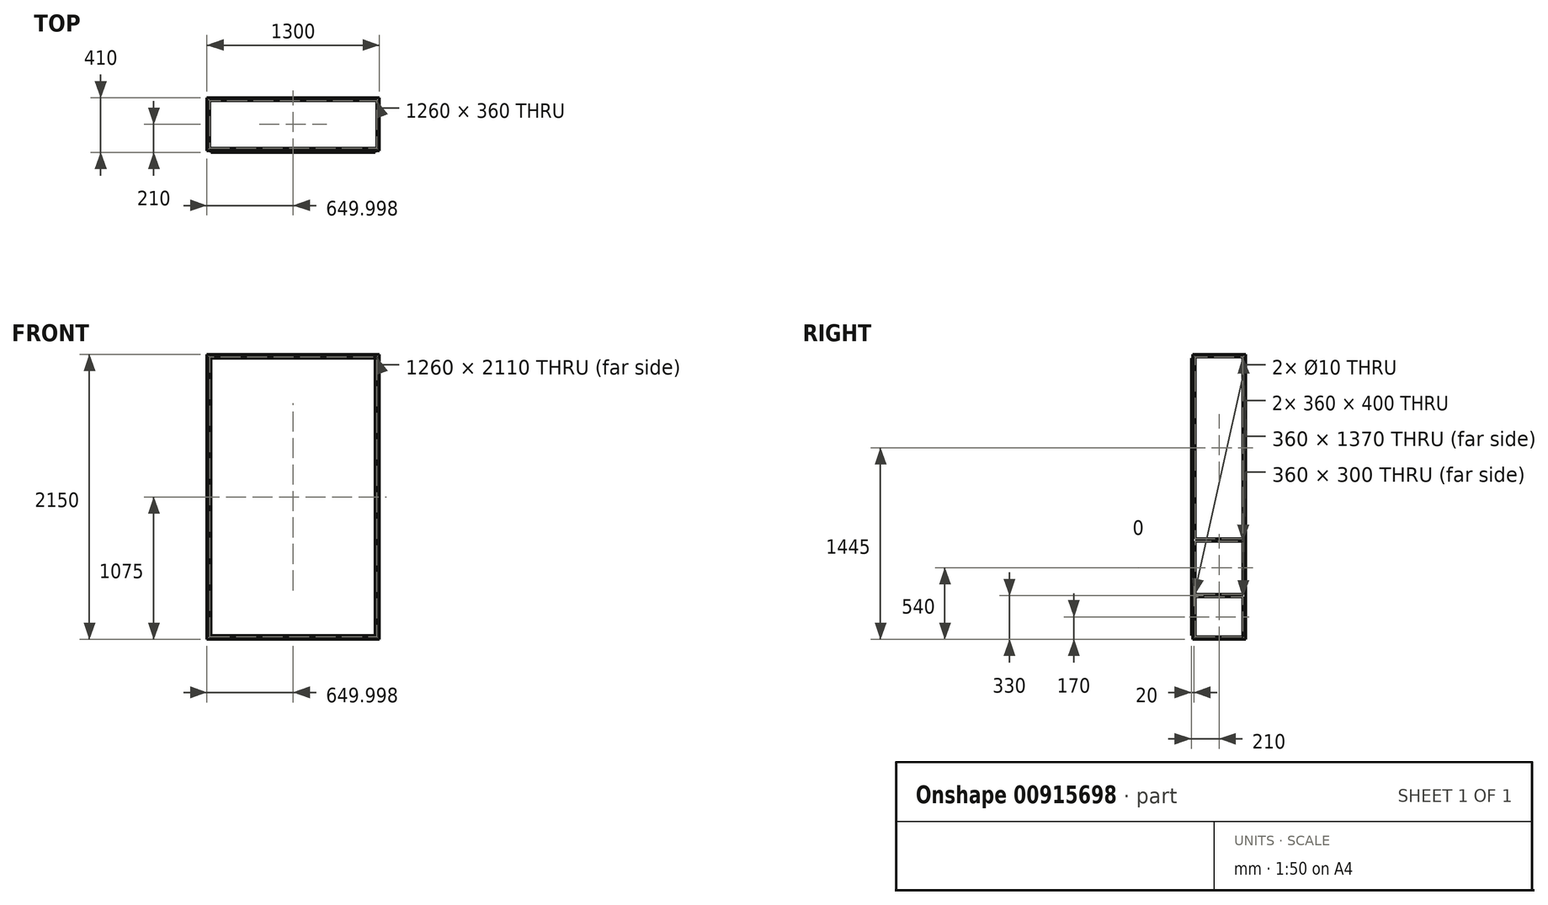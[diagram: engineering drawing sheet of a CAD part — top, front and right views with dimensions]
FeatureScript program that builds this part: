
annotation { "Feature Type Name" : "Feature", "Feature Type Description" : "" }
export const myFeature = defineFeature(function(context is Context, id is Id, definition is map)
    precondition{}
    {
        {
            var Q0;
            Q0=qCreatedBy(makeId("Front.planeOp"),FACE);
            var sketch = newSketch(context, id + "F0", { "sketchPlane" : qUnion([Q0])});
            skLineSegment(sketch, "E0", {"start": v(-54.92, 0) * mm, "end": v(1245.08, 0) * mm});
            skLineSegment(sketch, "E1", {"start": v(1245.08, 0) * mm, "end": v(1245.08, 2150) * mm});
            skLineSegment(sketch, "E2", {"start": v(1245.08, 2150) * mm, "end": v(-54.92, 2150) * mm});
            skLineSegment(sketch, "E3", {"start": v(-54.92, 0) * mm, "end": v(-54.92, 2150) * mm});
            skLineSegment(sketch, "E4.0", {"start": v(-34.92, 0) * mm, "end": v(-34.92, 2150) * mm});
            skLineSegment(sketch, "E5.0", {"start": v(1245.08, 2130) * mm, "end": v(-54.92, 2130) * mm});
            skLineSegment(sketch, "E6.0", {"start": v(1225.08, 0) * mm, "end": v(1225.08, 2150) * mm});
            skLineSegment(sketch, "E7.0", {"start": v(-54.92, 20) * mm, "end": v(1245.08, 20) * mm});
            skSolve(sketch);
        }
        {
            var Q0;
            {var subQ0=sQuery(id+"F0.wireOp",EDGE,"E4.0");var subQ1=sQuery(id+"F0.wireOp",EDGE,"E2");var subQ2=makeQuery(id+"F0.imprint","INTERSECT",VERTEX,{"derivedFrom":[subQ1,subQ0]});Q0=makeQuery(id+"F0.imprint","IMPRINT",FACE,{"disambiguationData":[TD([[makeQuery(id+"F0.imprint","IMPRINT",EDGE,{"disambiguationData":[TD([[subQ2,1.0]])],"derivedFrom":subQ1}),1.0]])]});}
            var Q1;
            {var subQ0=sQuery(id+"F0.wireOp",EDGE,"E3");var subQ1=sQuery(id+"F0.wireOp",EDGE,"E2");var subQ2=makeQuery(id+"F0.imprint","INTERSECT",VERTEX,{"derivedFrom":[subQ1,subQ0]});Q1=makeQuery(id+"F0.imprint","IMPRINT",FACE,{"disambiguationData":[TD([[makeQuery(id+"F0.imprint","IMPRINT",EDGE,{"disambiguationData":[TD([[subQ2,1.0]])],"derivedFrom":subQ1}),1.0]])]});}
            var Q2;
            {var subQ0=sQuery(id+"F0.wireOp",EDGE,"E5.0");var subQ1=sQuery(id+"F0.wireOp",EDGE,"E3");var subQ2=makeQuery(id+"F0.imprint","INTERSECT",VERTEX,{"derivedFrom":[subQ1,subQ0]});Q2=makeQuery(id+"F0.imprint","IMPRINT",FACE,{"disambiguationData":[TD([[makeQuery(id+"F0.imprint","IMPRINT",EDGE,{"disambiguationData":[TD([[subQ2,1.0]])],"derivedFrom":subQ1}),-1.0]])]});}
            var Q3;
            {var subQ0=sQuery(id+"F0.wireOp",EDGE,"E2");var subQ1=sQuery(id+"F0.wireOp",EDGE,"E1");var subQ2=makeQuery(id+"F0.imprint","INTERSECT",VERTEX,{"derivedFrom":[subQ1,subQ0]});Q3=makeQuery(id+"F0.imprint","IMPRINT",FACE,{"disambiguationData":[TD([[makeQuery(id+"F0.imprint","IMPRINT",EDGE,{"disambiguationData":[TD([[subQ2,1.0]])],"derivedFrom":subQ1}),1.0]])]});}
            var Q4;
            {var subQ0=sQuery(id+"F0.wireOp",EDGE,"E5.0");var subQ1=sQuery(id+"F0.wireOp",EDGE,"E1");var subQ2=makeQuery(id+"F0.imprint","INTERSECT",VERTEX,{"derivedFrom":[subQ1,subQ0]});Q4=makeQuery(id+"F0.imprint","IMPRINT",FACE,{"disambiguationData":[TD([[makeQuery(id+"F0.imprint","IMPRINT",EDGE,{"disambiguationData":[TD([[subQ2,1.0]])],"derivedFrom":subQ1}),1.0]])]});}
            var Q5;
            {var subQ0=sQuery(id+"F0.wireOp",EDGE,"E1");var subQ1=sQuery(id+"F0.wireOp",EDGE,"E0");var subQ2=makeQuery(id+"F0.imprint","INTERSECT",VERTEX,{"derivedFrom":[subQ1,subQ0]});Q5=makeQuery(id+"F0.imprint","IMPRINT",FACE,{"disambiguationData":[TD([[makeQuery(id+"F0.imprint","IMPRINT",EDGE,{"disambiguationData":[TD([[subQ2,1.0]])],"derivedFrom":subQ1}),1.0]])]});}
            var Q6;
            {var subQ0=sQuery(id+"F0.wireOp",EDGE,"E4.0");var subQ1=sQuery(id+"F0.wireOp",EDGE,"E0");var subQ2=makeQuery(id+"F0.imprint","INTERSECT",VERTEX,{"derivedFrom":[subQ1,subQ0]});Q6=makeQuery(id+"F0.imprint","IMPRINT",FACE,{"disambiguationData":[TD([[makeQuery(id+"F0.imprint","IMPRINT",EDGE,{"disambiguationData":[TD([[subQ2,-1.0]])],"derivedFrom":subQ1}),1.0]])]});}
            var Q7;
            {var subQ0=sQuery(id+"F0.wireOp",EDGE,"E3");var subQ1=sQuery(id+"F0.wireOp",EDGE,"E0");var subQ2=makeQuery(id+"F0.imprint","INTERSECT",VERTEX,{"derivedFrom":[subQ1,subQ0]});Q7=makeQuery(id+"F0.imprint","IMPRINT",FACE,{"disambiguationData":[TD([[makeQuery(id+"F0.imprint","IMPRINT",EDGE,{"disambiguationData":[TD([[subQ2,-1.0]])],"derivedFrom":subQ1}),1.0]])]});}
            extrude(context, id + "F1", {"entities" : qUnion([Q0, Q1, Q2, Q3, Q4, Q5, Q6, Q7]), "depth" : 20 * mm, "offsetDistance" : 25 * mm});
        }
        {
            var Q0;
            {var subQ0=sQuery(id+"F0.wireOp",EDGE,"E3");var subQ1=sQuery(id+"F0.wireOp",EDGE,"E0");var subQ2=makeQuery(id+"F0.imprint","INTERSECT",VERTEX,{"derivedFrom":[subQ1,subQ0]});Q0=makeQuery(id+"F0.imprint","IMPRINT",FACE,{"disambiguationData":[TD([[makeQuery(id+"F0.imprint","IMPRINT",EDGE,{"disambiguationData":[TD([[subQ2,-1.0]])],"derivedFrom":subQ1}),1.0]])]});}
            var Q1;
            {var subQ0=sQuery(id+"F0.wireOp",EDGE,"E1");var subQ1=sQuery(id+"F0.wireOp",EDGE,"E0");var subQ2=makeQuery(id+"F0.imprint","INTERSECT",VERTEX,{"derivedFrom":[subQ1,subQ0]});Q1=makeQuery(id+"F0.imprint","IMPRINT",FACE,{"disambiguationData":[TD([[makeQuery(id+"F0.imprint","IMPRINT",EDGE,{"disambiguationData":[TD([[subQ2,1.0]])],"derivedFrom":subQ1}),1.0]])]});}
            var Q2;
            {var subQ0=sQuery(id+"F0.wireOp",EDGE,"E3");var subQ1=sQuery(id+"F0.wireOp",EDGE,"E2");var subQ2=makeQuery(id+"F0.imprint","INTERSECT",VERTEX,{"derivedFrom":[subQ1,subQ0]});Q2=makeQuery(id+"F0.imprint","IMPRINT",FACE,{"disambiguationData":[TD([[makeQuery(id+"F0.imprint","IMPRINT",EDGE,{"disambiguationData":[TD([[subQ2,1.0]])],"derivedFrom":subQ1}),1.0]])]});}
            var Q3;
            {var subQ0=sQuery(id+"F0.wireOp",EDGE,"E2");var subQ1=sQuery(id+"F0.wireOp",EDGE,"E1");var subQ2=makeQuery(id+"F0.imprint","INTERSECT",VERTEX,{"derivedFrom":[subQ1,subQ0]});Q3=makeQuery(id+"F0.imprint","IMPRINT",FACE,{"disambiguationData":[TD([[makeQuery(id+"F0.imprint","IMPRINT",EDGE,{"disambiguationData":[TD([[subQ2,1.0]])],"derivedFrom":subQ1}),1.0]])]});}
            extrude(context, id + "F2", {"entities" : qUnion([Q0, Q1, Q2, Q3]), "operationType" : NewBodyOperationType.ADD, "depth" : 400 * mm, "offsetDistance" : 25 * mm});
        }
        {
            var Q0;
            Q0=makeQuery(id+"F2.opExtrude","CAP_FACE",FACE,{"disambiguationData":[OSD([sQuery(id+"F0.wireOp",EDGE,"E2"),sQuery(id+"F0.wireOp",EDGE,"E3"),sQuery(id+"F0.wireOp",EDGE,"E4.0"),sQuery(id+"F0.wireOp",EDGE,"E5.0")])],"isStart":false});
            var sketch = newSketch(context, id + "F3", { "sketchPlane" : qUnion([Q0])});
            skLineSegment(sketch, "E8.0", {"start": v(1245.08, 2130) * mm, "end": v(-54.92, 2130) * mm});
            skLineSegment(sketch, "E9.0", {"start": v(1245.08, 2150) * mm, "end": v(-54.92, 2150) * mm});
            skLineSegment(sketch, "E10.0", {"start": v(1225.08, 0) * mm, "end": v(1225.08, 2150) * mm});
            skLineSegment(sketch, "E11.0", {"start": v(1245.08, 0) * mm, "end": v(1245.08, 2150) * mm});
            skLineSegment(sketch, "E12.0", {"start": v(-54.92, 20) * mm, "end": v(1245.08, 20) * mm});
            skLineSegment(sketch, "E13.0", {"start": v(-54.92, 0) * mm, "end": v(1245.08, 0) * mm});
            skLineSegment(sketch, "E14.0", {"start": v(-34.92, 0) * mm, "end": v(-34.92, 2150) * mm});
            skLineSegment(sketch, "E15.0", {"start": v(-54.92, 0) * mm, "end": v(-54.92, 2150) * mm});
            skSolve(sketch);
        }
        {
            var Q0;
            {var subQ0=sQuery(id+"F3.wireOp",EDGE,"E15.0");var subQ1=sQuery(id+"F3.wireOp",EDGE,"E8.0");var subQ2=makeQuery(id+"F3.imprint","INTERSECT",VERTEX,{"derivedFrom":[subQ1,subQ0]});Q0=makeQuery(id+"F3.imprint","IMPRINT",FACE,{"disambiguationData":[TD([[makeQuery(id+"F3.imprint","IMPRINT",EDGE,{"disambiguationData":[TD([[subQ2,1.0]])],"derivedFrom":subQ1}),1.0]])]});}
            var Q1;
            {var subQ0=sQuery(id+"F3.wireOp",EDGE,"E13.0");var subQ1=sQuery(id+"F3.wireOp",EDGE,"E10.0");var subQ2=makeQuery(id+"F3.imprint","INTERSECT",VERTEX,{"derivedFrom":[subQ1,subQ0]});Q1=makeQuery(id+"F3.imprint","IMPRINT",FACE,{"disambiguationData":[TD([[makeQuery(id+"F3.imprint","IMPRINT",EDGE,{"disambiguationData":[TD([[subQ2,-1.0]])],"derivedFrom":subQ1}),1.0]])]});}
            var Q2;
            {var subQ0=sQuery(id+"F3.wireOp",EDGE,"E11.0");var subQ1=sQuery(id+"F3.wireOp",EDGE,"E8.0");var subQ2=makeQuery(id+"F3.imprint","INTERSECT",VERTEX,{"derivedFrom":[subQ1,subQ0]});Q2=makeQuery(id+"F3.imprint","IMPRINT",FACE,{"disambiguationData":[TD([[makeQuery(id+"F3.imprint","IMPRINT",EDGE,{"disambiguationData":[TD([[subQ2,-1.0]])],"derivedFrom":subQ1}),1.0]])]});}
            var Q3;
            {var subQ0=sQuery(id+"F3.wireOp",EDGE,"E14.0");var subQ1=sQuery(id+"F3.wireOp",EDGE,"E8.0");var subQ2=makeQuery(id+"F3.imprint","INTERSECT",VERTEX,{"derivedFrom":[subQ1,subQ0]});Q3=makeQuery(id+"F3.imprint","IMPRINT",FACE,{"disambiguationData":[TD([[makeQuery(id+"F3.imprint","IMPRINT",EDGE,{"disambiguationData":[TD([[subQ2,1.0]])],"derivedFrom":subQ1}),-1.0]])]});}
            extrude(context, id + "F4", {"entities" : qUnion([Q0, Q1, Q2, Q3]), "operationType" : NewBodyOperationType.ADD, "oppositeDirection" : true, "depth" : 20 * mm, "offsetDistance" : 25 * mm});
        }
        {
            var Q0;
            {var subQ0=sQuery(id+"F0.wireOp",EDGE,"E1");Q0=makeQuery(id+"F4.boolean.opBoolean","MERGE",FACE,{"derivedFrom":[makeQuery(id+"F2.boolean.opBoolean","MERGE",FACE,{"derivedFrom":[makeQuery(id+"F1.opExtrude","SWEPT_FACE",FACE,{"disambiguationData":[OSD([subQ0])]}),makeQuery(id+"F2.opExtrude","SWEPT_FACE",FACE,{"disambiguationData":[OSD([subQ0]),TDD([makeQuery(id+"F0.imprint","IMPRINT",EDGE,{"disambiguationData":[TD([[makeQuery(id+"F0.imprint","INTERSECT",VERTEX,{"derivedFrom":[sQuery(id+"F0.wireOp",EDGE,"E0"),subQ0]}),-1.0]])],"derivedFrom":subQ0})])]}),makeQuery(id+"F2.opExtrude","SWEPT_FACE",FACE,{"disambiguationData":[OSD([subQ0]),TDD([makeQuery(id+"F0.imprint","IMPRINT",EDGE,{"disambiguationData":[TD([[makeQuery(id+"F0.imprint","INTERSECT",VERTEX,{"derivedFrom":[subQ0,sQuery(id+"F0.wireOp",EDGE,"E2")]}),1.0]])],"derivedFrom":subQ0})])]})]}),makeQuery(id+"F4.opExtrude","SWEPT_FACE",FACE,{"disambiguationData":[OSD([sQuery(id+"F3.wireOp",EDGE,"E11.0")])]})]});}
            var sketch = newSketch(context, id + "F5", { "sketchPlane" : qUnion([Q0])});
            skLineSegment(sketch, "E16.0", {"start": v(-400, 340) * mm, "end": v(0, 340) * mm});
            skLineSegment(sketch, "E17.0", {"start": v(-400, 320) * mm, "end": v(0, 320) * mm});
            skLineSegment(sketch, "E18", {"start": v(-400, 340) * mm, "end": v(-400, 320) * mm});
            skLineSegment(sketch, "E19", {"start": v(0, 340) * mm, "end": v(0, 320) * mm});
            skLineSegment(sketch, "E20.0", {"start": v(-400, 740) * mm, "end": v(0, 740) * mm});
            skLineSegment(sketch, "E21.0", {"start": v(-400, 760) * mm, "end": v(0, 760) * mm});
            skLineSegment(sketch, "E22", {"start": v(0, 760) * mm, "end": v(0, 740) * mm});
            skLineSegment(sketch, "E23", {"start": v(-400, 760) * mm, "end": v(-400, 740) * mm});
            skSolve(sketch);
        }
        {
            var Q0;
            Q0=qSketchRegion(id+"F5",true);
            extrude(context, id + "F6", {"entities" : qUnion([Q0]), "operationType" : NewBodyOperationType.ADD, "oppositeDirection" : true, "depth" : 20 * mm, "offsetDistance" : 25 * mm});
        }
        {
            var Q0;
            Q0=qSketchRegion(id+"F5",true);
            extrude(context, id + "F7", {"entities" : qUnion([Q0]), "operationType" : NewBodyOperationType.ADD, "oppositeDirection" : true, "depth" : 20 * mm, "offsetDistance" : 25 * mm});
        }
        {
            var Q0;
            {var subQ0=sQuery(id+"F0.wireOp",EDGE,"E3");Q0=makeQuery(id+"F4.boolean.opBoolean","MERGE",FACE,{"derivedFrom":[makeQuery(id+"F2.boolean.opBoolean","MERGE",FACE,{"derivedFrom":[makeQuery(id+"F1.opExtrude","SWEPT_FACE",FACE,{"disambiguationData":[OSD([subQ0])]}),makeQuery(id+"F2.opExtrude","SWEPT_FACE",FACE,{"disambiguationData":[OSD([subQ0]),TDD([makeQuery(id+"F0.imprint","IMPRINT",EDGE,{"disambiguationData":[TD([[makeQuery(id+"F0.imprint","INTERSECT",VERTEX,{"derivedFrom":[sQuery(id+"F0.wireOp",EDGE,"E0"),subQ0]}),-1.0]])],"derivedFrom":subQ0})])]}),makeQuery(id+"F2.opExtrude","SWEPT_FACE",FACE,{"disambiguationData":[OSD([subQ0]),TDD([makeQuery(id+"F0.imprint","IMPRINT",EDGE,{"disambiguationData":[TD([[makeQuery(id+"F0.imprint","INTERSECT",VERTEX,{"derivedFrom":[sQuery(id+"F0.wireOp",EDGE,"E2"),subQ0]}),1.0]])],"derivedFrom":subQ0})])]})]}),makeQuery(id+"F4.opExtrude","SWEPT_FACE",FACE,{"disambiguationData":[OSD([sQuery(id+"F3.wireOp",EDGE,"E15.0")])]})]});}
            var sketch = newSketch(context, id + "F8", { "sketchPlane" : qUnion([Q0])});
            skLineSegment(sketch, "E24.0", {"start": v(380, 320) * mm, "end": v(20, 320) * mm});
            skLineSegment(sketch, "E25.0", {"start": v(380, 340) * mm, "end": v(20, 340) * mm});
            skLineSegment(sketch, "E26.0", {"start": v(380, 740) * mm, "end": v(20, 740) * mm});
            skLineSegment(sketch, "E27.0", {"start": v(380, 760) * mm, "end": v(20, 760) * mm});
            skLineSegment(sketch, "E28", {"start": v(20, 760) * mm, "end": v(20, 320) * mm});
            skLineSegment(sketch, "E29", {"start": v(380, 320) * mm, "end": v(380, 760) * mm});
            skSolve(sketch);
        }
        {
            var Q0;
            {var subQ0=sQuery(id+"F8.wireOp",EDGE,"E26.0");Q0=makeQuery(id+"F8.imprint","IMPRINT",FACE,{"disambiguationData":[TD([[makeQuery(id+"F8.imprint","IMPRINT",EDGE,{"derivedFrom":subQ0}),-1.0]])]});}
            var Q1;
            {var subQ0=sQuery(id+"F8.wireOp",EDGE,"E24.0");Q1=makeQuery(id+"F8.imprint","IMPRINT",FACE,{"disambiguationData":[TD([[makeQuery(id+"F8.imprint","IMPRINT",EDGE,{"derivedFrom":subQ0}),-1.0]])]});}
            extrude(context, id + "F9", {"entities" : qUnion([Q0, Q1]), "operationType" : NewBodyOperationType.ADD, "oppositeDirection" : true, "depth" : 20 * mm, "offsetDistance" : 25 * mm});
        }
        {
            var Q0;
            {var subQ0=sQuery(id+"F0.wireOp",EDGE,"E1");Q0=makeQuery(id+"F6.boolean.opBoolean","MERGE",FACE,{"derivedFrom":[makeQuery(id+"F4.boolean.opBoolean","MERGE",FACE,{"derivedFrom":[makeQuery(id+"F2.boolean.opBoolean","MERGE",FACE,{"derivedFrom":[makeQuery(id+"F1.opExtrude","SWEPT_FACE",FACE,{"disambiguationData":[OSD([subQ0])]}),makeQuery(id+"F2.opExtrude","SWEPT_FACE",FACE,{"disambiguationData":[OSD([subQ0]),TDD([makeQuery(id+"F0.imprint","IMPRINT",EDGE,{"disambiguationData":[TD([[makeQuery(id+"F0.imprint","INTERSECT",VERTEX,{"derivedFrom":[sQuery(id+"F0.wireOp",EDGE,"E0"),subQ0]}),-1.0]])],"derivedFrom":subQ0})])]}),makeQuery(id+"F2.opExtrude","SWEPT_FACE",FACE,{"disambiguationData":[OSD([subQ0]),TDD([makeQuery(id+"F0.imprint","IMPRINT",EDGE,{"disambiguationData":[TD([[makeQuery(id+"F0.imprint","INTERSECT",VERTEX,{"derivedFrom":[subQ0,sQuery(id+"F0.wireOp",EDGE,"E2")]}),1.0]])],"derivedFrom":subQ0})])]})]}),makeQuery(id+"F4.opExtrude","SWEPT_FACE",FACE,{"disambiguationData":[OSD([sQuery(id+"F3.wireOp",EDGE,"E11.0")])]})]}),makeQuery(id+"F6.opExtrude","CAP_FACE",FACE,{"disambiguationData":[OSD([sQuery(id+"F5.wireOp",EDGE,"E16.0"),sQuery(id+"F5.wireOp",EDGE,"E17.0"),sQuery(id+"F5.wireOp",EDGE,"E18"),sQuery(id+"F5.wireOp",EDGE,"E19")])],"isStart":true}),makeQuery(id+"F6.opExtrude","CAP_FACE",FACE,{"disambiguationData":[OSD([sQuery(id+"F5.wireOp",EDGE,"E20.0"),sQuery(id+"F5.wireOp",EDGE,"E21.0"),sQuery(id+"F5.wireOp",EDGE,"E22"),sQuery(id+"F5.wireOp",EDGE,"E23")])],"isStart":true})]});}
            var sketch = newSketch(context, id + "F10", { "sketchPlane" : qUnion([Q0])});
            skLineSegment(sketch, "E30.0", {"start": v(-531.42, 330) * mm, "end": v(-20, 330) * mm, "construction": true});
            skLineSegment(sketch, "E31.0", {"start": v(-390, 0) * mm, "end": v(-390, 2150) * mm, "construction": true});
            skCircle(sketch, "E32", {"center": v(-390, 330) * mm, "radius": 5 * mm});
            skSolve(sketch);
        }
        {
            var Q0;
            Q0=qSketchRegion(id+"F10",true);
            extrude(context, id + "F11", {"entities" : qUnion([Q0]), "operationType" : NewBodyOperationType.REMOVE, "endBound" : BoundingType.THROUGH_ALL, "oppositeDirection" : true, "depth" : 25 * mm, "offsetDistance" : 25 * mm});
        }
        {
            var Q0;
            {var subQ0=sQuery(id+"F3.wireOp",EDGE,"E14.0");var subQ1=sQuery(id+"F3.wireOp",EDGE,"E12.0");var subQ2=sQuery(id+"F3.wireOp",EDGE,"E10.0");var subQ3=sQuery(id+"F3.wireOp",EDGE,"E8.0");var subQ4=sQuery(id+"F0.wireOp",EDGE,"E5.0");var subQ5=sQuery(id+"F0.wireOp",EDGE,"E4.0");var subQ6=sQuery(id+"F0.wireOp",EDGE,"E3");var subQ7=sQuery(id+"F0.wireOp",EDGE,"E2");var subQ8=sQuery(id+"F0.wireOp",EDGE,"E6.0");var subQ9=sQuery(id+"F0.wireOp",EDGE,"E1");var subQ10=sQuery(id+"F0.wireOp",EDGE,"E7.0");var subQ11=sQuery(id+"F0.wireOp",EDGE,"E0");Q0=makeQuery(id+"F4.boolean.opBoolean","MERGE",FACE,{"derivedFrom":[makeQuery(id+"F2.opExtrude","CAP_FACE",FACE,{"disambiguationData":[OSD([subQ11,subQ6,subQ5,subQ10])],"isStart":false}),makeQuery(id+"F2.opExtrude","CAP_FACE",FACE,{"disambiguationData":[OSD([subQ11,subQ9,subQ8,subQ10])],"isStart":false}),makeQuery(id+"F2.opExtrude","CAP_FACE",FACE,{"disambiguationData":[OSD([subQ9,subQ7,subQ4,subQ8])],"isStart":false}),makeQuery(id+"F2.opExtrude","CAP_FACE",FACE,{"disambiguationData":[OSD([subQ7,subQ6,subQ5,subQ4])],"isStart":false}),makeQuery(id+"F4.opExtrude","CAP_FACE",FACE,{"disambiguationData":[OSD([subQ3,subQ2,sQuery(id+"F3.wireOp",EDGE,"E11.0"),subQ1])],"isStart":true}),makeQuery(id+"F4.opExtrude","CAP_FACE",FACE,{"disambiguationData":[OSD([subQ3,sQuery(id+"F3.wireOp",EDGE,"E9.0"),subQ2,subQ0])],"isStart":true}),makeQuery(id+"F4.opExtrude","CAP_FACE",FACE,{"disambiguationData":[OSD([subQ3,subQ1,subQ0,sQuery(id+"F3.wireOp",EDGE,"E15.0")])],"isStart":true}),makeQuery(id+"F4.opExtrude","CAP_FACE",FACE,{"disambiguationData":[OSD([subQ2,subQ1,sQuery(id+"F3.wireOp",EDGE,"E13.0"),subQ0])],"isStart":true})]});}
            var sketch = newSketch(context, id + "F12", { "sketchPlane" : qUnion([Q0])});
            skLineSegment(sketch, "E33.0", {"start": v(1245.08, 2120) * mm, "end": v(-54.92, 2120) * mm});
            skLineSegment(sketch, "E34.0", {"start": v(1215.08, 0) * mm, "end": v(1215.08, 2150) * mm});
            skLineSegment(sketch, "E35.0", {"start": v(-54.92, 30) * mm, "end": v(1245.08, 30) * mm});
            skLineSegment(sketch, "E36.0", {"start": v(-24.92, 0) * mm, "end": v(-24.92, 2150) * mm});
            skLineSegment(sketch, "E37.0", {"start": v(1245.08, 2100) * mm, "end": v(-54.92, 2100) * mm});
            skLineSegment(sketch, "E38.0", {"start": v(1195.08, 0) * mm, "end": v(1195.08, 2150) * mm});
            skLineSegment(sketch, "E39.0", {"start": v(-54.92, 50) * mm, "end": v(1245.08, 50) * mm});
            skLineSegment(sketch, "E40.0", {"start": v(-4.92, 0) * mm, "end": v(-4.92, 2150) * mm});
            skSolve(sketch);
        }
        {
            var Q0;
            Q0 = qSketchRegion(id + "F12", true);
            var Q1;
            {var subQ0=sQuery(id+"F12.wireOp",EDGE,"E38.0");var subQ1=sQuery(id+"F12.wireOp",EDGE,"E37.0");var subQ2=makeQuery(id+"F12.imprint","INTERSECT",VERTEX,{"derivedFrom":[subQ1,subQ0]});Q1=makeQuery(id+"F12.imprint","IMPRINT",FACE,{"disambiguationData":[TD([[makeQuery(id+"F12.imprint","IMPRINT",EDGE,{"disambiguationData":[TD([[subQ2,-1.0]])],"derivedFrom":subQ1}),1.0]])]});}
            extrude(context, id + "F13", {"entities" : qUnion([Q0, Q1]), "depth" : 10 * mm, "offsetDistance" : 25 * mm});
        }
    });
